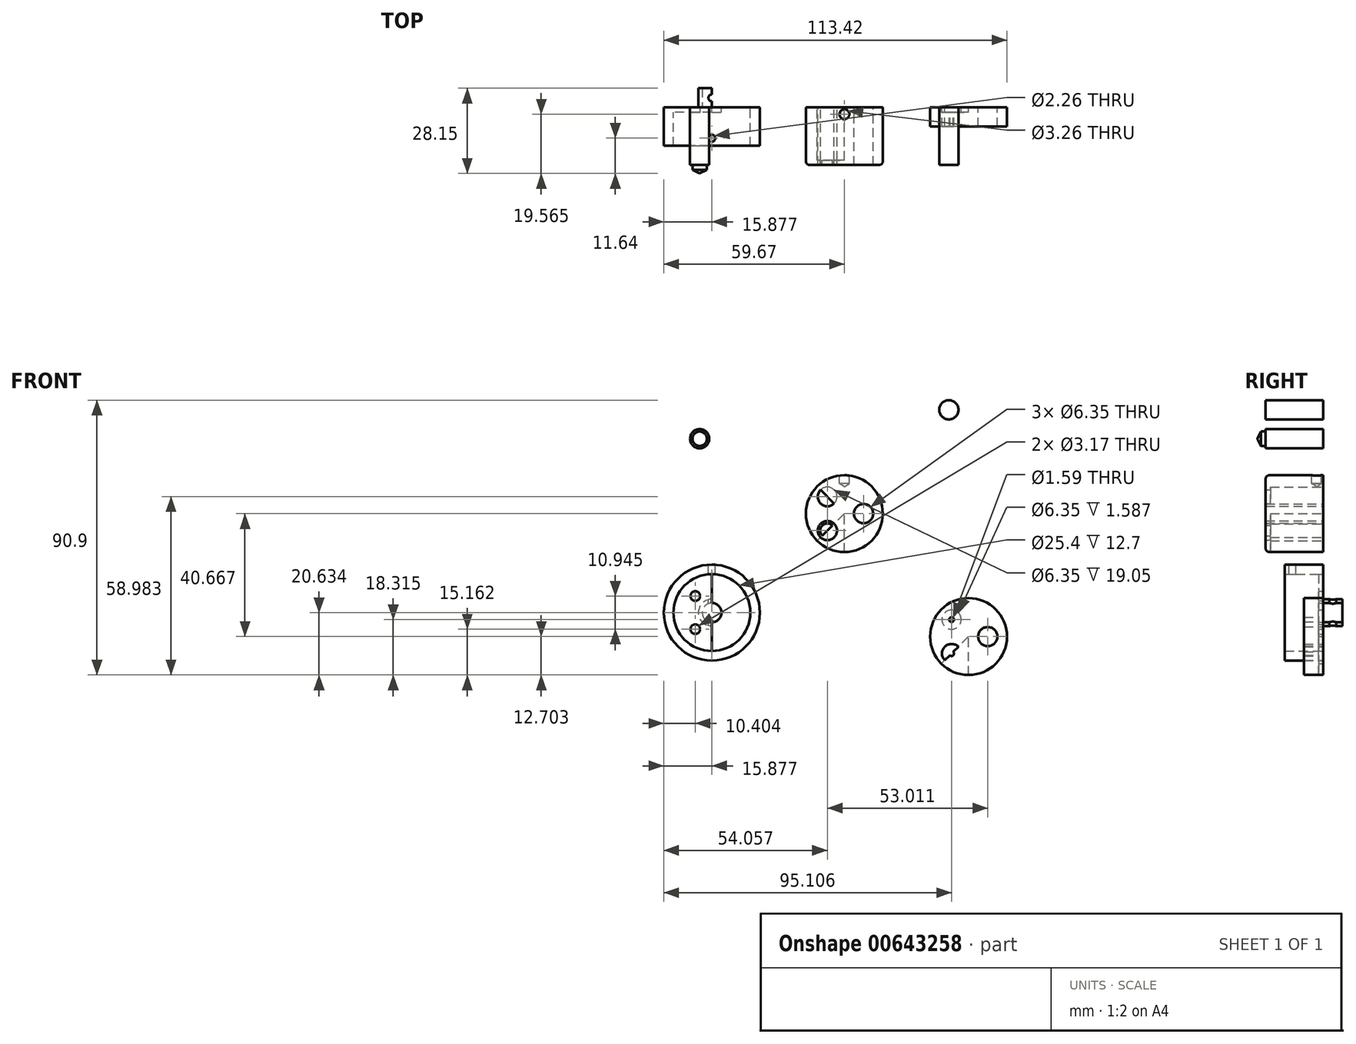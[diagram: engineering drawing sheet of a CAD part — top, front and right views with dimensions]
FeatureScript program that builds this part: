
annotation { "Feature Type Name" : "Feature", "Feature Type Description" : "" }
export const myFeature = defineFeature(function(context is Context, id is Id, definition is map)
    precondition{}
    {
        {
            var Q0;
            Q0=qCreatedBy(makeId("Front.planeOp"),FACE);
            var sketch = newSketch(context, id + "F0", { "sketchPlane" : qUnion([Q0])});
            skCircle(sketch, "E0", {"center": v(0, 0) * mm, "radius": 12.7 * mm});
            skLineSegment(sketch, "E1", {"start": v(0, 0) * mm, "end": v(12.7, 0) * mm});
            skLineSegment(sketch, "E2", {"start": v(12.7, 0) * mm, "end": v(0, 0) * mm});
            skLineSegment(sketch, "E3", {"start": v(0, 12.7) * mm, "end": v(0, 0) * mm});
            skLineSegment(sketch, "E4", {"start": v(0, -12.7) * mm, "end": v(0, 0) * mm});
            skLineSegment(sketch, "E5", {"start": v(-12.7, 0) * mm, "end": v(0, 0) * mm});
            skLineSegment(sketch, "E6", {"start": v(0, 12.7) * mm, "end": v(-12.7, 0) * mm});
            skLineSegment(sketch, "E7", {"start": v(-12.7, 0) * mm, "end": v(0, -12.7) * mm});
            skLineSegment(sketch, "E8", {"start": v(0, 0) * mm, "end": v(-8.98, -8.98) * mm});
            skLineSegment(sketch, "E9", {"start": v(-8.98, -8.98) * mm, "end": v(-8.98, 8.98) * mm});
            skLineSegment(sketch, "E10", {"start": v(-8.98, 8.98) * mm, "end": v(0, 0) * mm});
            skCircle(sketch, "E11", {"center": v(6.35, 0) * mm, "radius": 3.18 * mm});
            skCircle(sketch, "E12", {"center": v(6.35, 0) * mm, "radius": 2.38 * mm});
            skCircle(sketch, "E13", {"center": v(-5.61, 5.61) * mm, "radius": 3.18 * mm});
            skCircle(sketch, "E14", {"center": v(-5.61, -5.61) * mm, "radius": 3.18 * mm});
            skCircle(sketch, "E15", {"center": v(-5.61, 5.61) * mm, "radius": 2.38 * mm});
            skCircle(sketch, "E16", {"center": v(-5.61, -5.61) * mm, "radius": 2.38 * mm});
            skSolve(sketch);
        }
        {
            var Q0;
            {var subQ0=sQuery(id+"F0.wireOp",EDGE,"E4");Q0=makeQuery(id+"F0.imprint","IMPRINT",FACE,{"disambiguationData":[TD([[makeQuery(id+"F0.imprint","IMPRINT",EDGE,{"derivedFrom":subQ0}),-1.0]])]});}
            var Q1;
            {var subQ0=sQuery(id+"F0.wireOp",EDGE,"E3");Q1=makeQuery(id+"F0.imprint","IMPRINT",FACE,{"disambiguationData":[TD([[makeQuery(id+"F0.imprint","IMPRINT",EDGE,{"derivedFrom":subQ0}),1.0]])]});}
            var Q2;
            {var subQ0=sQuery(id+"F0.wireOp",EDGE,"E12");var subQ1=sQuery(id+"F0.wireOp",EDGE,"E2");var subQ2=makeQuery(id+"F0.imprint","INTERSECT",VERTEX,{"disambiguationData":[OD(0.0)],"derivedFrom":[subQ1,subQ0]});Q2=makeQuery(id+"F0.imprint","IMPRINT",FACE,{"disambiguationData":[TD([[makeQuery(id+"F0.imprint","IMPRINT",EDGE,{"disambiguationData":[TD([[subQ2,-1.0]])],"derivedFrom":subQ1}),1.0]])]});}
            var Q3;
            {var subQ0=sQuery(id+"F0.wireOp",EDGE,"E12");var subQ1=sQuery(id+"F0.wireOp",EDGE,"E2");var subQ2=makeQuery(id+"F0.imprint","INTERSECT",VERTEX,{"disambiguationData":[OD(0.0)],"derivedFrom":[subQ1,subQ0]});Q3=makeQuery(id+"F0.imprint","IMPRINT",FACE,{"disambiguationData":[TD([[makeQuery(id+"F0.imprint","IMPRINT",EDGE,{"disambiguationData":[TD([[subQ2,-1.0]])],"derivedFrom":subQ1}),-1.0]])]});}
            var Q4;
            {var subQ0=sQuery(id+"F0.wireOp",EDGE,"E11");var subQ1=sQuery(id+"F0.wireOp",EDGE,"E2");var subQ2=makeQuery(id+"F0.imprint","INTERSECT",VERTEX,{"disambiguationData":[OD(0.0)],"derivedFrom":[subQ1,subQ0]});Q4=makeQuery(id+"F0.imprint","IMPRINT",FACE,{"disambiguationData":[TD([[makeQuery(id+"F0.imprint","IMPRINT",EDGE,{"disambiguationData":[TD([[subQ2,-1.0]])],"derivedFrom":subQ1}),1.0]])]});}
            var Q5;
            {var subQ0=sQuery(id+"F0.wireOp",EDGE,"E11");var subQ1=sQuery(id+"F0.wireOp",EDGE,"E2");var subQ2=makeQuery(id+"F0.imprint","INTERSECT",VERTEX,{"disambiguationData":[OD(0.0)],"derivedFrom":[subQ1,subQ0]});Q5=makeQuery(id+"F0.imprint","IMPRINT",FACE,{"disambiguationData":[TD([[makeQuery(id+"F0.imprint","IMPRINT",EDGE,{"disambiguationData":[TD([[subQ2,-1.0]])],"derivedFrom":subQ1}),-1.0]])]});}
            var Q6;
            {var subQ0=sQuery(id+"F0.wireOp",EDGE,"E3");Q6=makeQuery(id+"F0.imprint","IMPRINT",FACE,{"disambiguationData":[TD([[makeQuery(id+"F0.imprint","IMPRINT",EDGE,{"derivedFrom":subQ0}),-1.0]])]});}
            var Q7;
            {var subQ0=sQuery(id+"F0.wireOp",EDGE,"E4");Q7=makeQuery(id+"F0.imprint","IMPRINT",FACE,{"disambiguationData":[TD([[makeQuery(id+"F0.imprint","IMPRINT",EDGE,{"derivedFrom":subQ0}),1.0]])]});}
            var Q8;
            {var subQ0=sQuery(id+"F0.wireOp",EDGE,"E7");var subQ5=sQuery(id+"F0.wireOp",EDGE,"E14");var subQ7=makeQuery(id+"F0.imprint","INTERSECT",VERTEX,{"disambiguationData":[OD(1.0)],"derivedFrom":[subQ0,subQ5]});Q8=makeQuery(id+"F0.imprint","IMPRINT",FACE,{"disambiguationData":[TD([[makeQuery(id+"F0.imprint","IMPRINT",EDGE,{"disambiguationData":[TD([[subQ7,1.0]])],"derivedFrom":subQ5}),-1.0]])]});}
            var Q9;
            {var subQ0=sQuery(id+"F0.wireOp",EDGE,"E8");var subQ1=sQuery(id+"F0.wireOp",EDGE,"E7");var subQ2=makeQuery(id+"F0.imprint","INTERSECT",VERTEX,{"derivedFrom":[subQ1,subQ0]});Q9=makeQuery(id+"F0.imprint","IMPRINT",FACE,{"disambiguationData":[TD([[makeQuery(id+"F0.imprint","IMPRINT",EDGE,{"disambiguationData":[TD([[subQ2,-1.0]])],"derivedFrom":subQ1}),1.0]])]});}
            var Q10;
            {var subQ0=sQuery(id+"F0.wireOp",EDGE,"E16");var subQ1=sQuery(id+"F0.wireOp",EDGE,"E7");var subQ2=makeQuery(id+"F0.imprint","INTERSECT",VERTEX,{"disambiguationData":[OD(0.0)],"derivedFrom":[subQ1,subQ0]});Q10=makeQuery(id+"F0.imprint","IMPRINT",FACE,{"disambiguationData":[TD([[makeQuery(id+"F0.imprint","IMPRINT",EDGE,{"disambiguationData":[TD([[subQ2,-1.0]])],"derivedFrom":subQ1}),1.0]])]});}
            var Q11;
            {var subQ0=sQuery(id+"F0.wireOp",EDGE,"E8");var subQ1=sQuery(id+"F0.wireOp",EDGE,"E7");var subQ2=makeQuery(id+"F0.imprint","INTERSECT",VERTEX,{"derivedFrom":[subQ1,subQ0]});Q11=makeQuery(id+"F0.imprint","IMPRINT",FACE,{"disambiguationData":[TD([[makeQuery(id+"F0.imprint","IMPRINT",EDGE,{"disambiguationData":[TD([[subQ2,-1.0]])],"derivedFrom":subQ1}),-1.0]])]});}
            var Q12;
            {var subQ0=sQuery(id+"F0.wireOp",EDGE,"E16");var subQ1=sQuery(id+"F0.wireOp",EDGE,"E7");var subQ2=makeQuery(id+"F0.imprint","INTERSECT",VERTEX,{"disambiguationData":[OD(0.0)],"derivedFrom":[subQ1,subQ0]});Q12=makeQuery(id+"F0.imprint","IMPRINT",FACE,{"disambiguationData":[TD([[makeQuery(id+"F0.imprint","IMPRINT",EDGE,{"disambiguationData":[TD([[subQ2,-1.0]])],"derivedFrom":subQ1}),-1.0]])]});}
            var Q13;
            {var subQ0=sQuery(id+"F0.wireOp",EDGE,"E9");var subQ3=sQuery(id+"F0.wireOp",EDGE,"E7");var subQ4=makeQuery(id+"F0.imprint","INTERSECT",VERTEX,{"derivedFrom":[subQ3,subQ0]});Q13=makeQuery(id+"F0.imprint","IMPRINT",FACE,{"disambiguationData":[TD([[makeQuery(id+"F0.imprint","IMPRINT",EDGE,{"disambiguationData":[TD([[subQ4,-1.0]])],"derivedFrom":subQ3}),1.0]])]});}
            var Q14;
            {var subQ3=sQuery(id+"F0.wireOp",EDGE,"E6");var subQ5=sQuery(id+"F0.wireOp",EDGE,"E13");var subQ6=makeQuery(id+"F0.imprint","INTERSECT",VERTEX,{"disambiguationData":[OD(1.0)],"derivedFrom":[subQ3,subQ5]});Q14=makeQuery(id+"F0.imprint","IMPRINT",FACE,{"disambiguationData":[TD([[makeQuery(id+"F0.imprint","IMPRINT",EDGE,{"disambiguationData":[TD([[subQ6,-1.0]])],"derivedFrom":subQ3}),1.0]])]});}
            var Q15;
            {var subQ0=sQuery(id+"F0.wireOp",EDGE,"E10");var subQ1=sQuery(id+"F0.wireOp",EDGE,"E6");var subQ2=makeQuery(id+"F0.imprint","INTERSECT",VERTEX,{"derivedFrom":[subQ1,subQ0]});Q15=makeQuery(id+"F0.imprint","IMPRINT",FACE,{"disambiguationData":[TD([[makeQuery(id+"F0.imprint","IMPRINT",EDGE,{"disambiguationData":[TD([[subQ2,-1.0]])],"derivedFrom":subQ1}),1.0]])]});}
            var Q16;
            {var subQ0=sQuery(id+"F0.wireOp",EDGE,"E15");var subQ1=sQuery(id+"F0.wireOp",EDGE,"E6");var subQ2=makeQuery(id+"F0.imprint","INTERSECT",VERTEX,{"disambiguationData":[OD(0.0)],"derivedFrom":[subQ1,subQ0]});Q16=makeQuery(id+"F0.imprint","IMPRINT",FACE,{"disambiguationData":[TD([[makeQuery(id+"F0.imprint","IMPRINT",EDGE,{"disambiguationData":[TD([[subQ2,-1.0]])],"derivedFrom":subQ1}),1.0]])]});}
            var Q17;
            {var subQ0=sQuery(id+"F0.wireOp",EDGE,"E15");var subQ1=sQuery(id+"F0.wireOp",EDGE,"E6");var subQ2=makeQuery(id+"F0.imprint","INTERSECT",VERTEX,{"disambiguationData":[OD(0.0)],"derivedFrom":[subQ1,subQ0]});Q17=makeQuery(id+"F0.imprint","IMPRINT",FACE,{"disambiguationData":[TD([[makeQuery(id+"F0.imprint","IMPRINT",EDGE,{"disambiguationData":[TD([[subQ2,-1.0]])],"derivedFrom":subQ1}),-1.0]])]});}
            var Q18;
            {var subQ0=sQuery(id+"F0.wireOp",EDGE,"E10");var subQ1=sQuery(id+"F0.wireOp",EDGE,"E6");var subQ2=makeQuery(id+"F0.imprint","INTERSECT",VERTEX,{"derivedFrom":[subQ1,subQ0]});Q18=makeQuery(id+"F0.imprint","IMPRINT",FACE,{"disambiguationData":[TD([[makeQuery(id+"F0.imprint","IMPRINT",EDGE,{"disambiguationData":[TD([[subQ2,-1.0]])],"derivedFrom":subQ1}),-1.0]])]});}
            var Q19;
            {var subQ0=sQuery(id+"F0.wireOp",EDGE,"E13");var subQ1=sQuery(id+"F0.wireOp",EDGE,"E6");var subQ2=makeQuery(id+"F0.imprint","INTERSECT",VERTEX,{"disambiguationData":[OD(0.0)],"derivedFrom":[subQ1,subQ0]});Q19=makeQuery(id+"F0.imprint","IMPRINT",FACE,{"disambiguationData":[TD([[makeQuery(id+"F0.imprint","IMPRINT",EDGE,{"disambiguationData":[TD([[subQ2,-1.0]])],"derivedFrom":subQ1}),-1.0]])]});}
            var Q20;
            {var subQ0=sQuery(id+"F0.wireOp",EDGE,"E13");var subQ1=sQuery(id+"F0.wireOp",EDGE,"E6");var subQ2=makeQuery(id+"F0.imprint","INTERSECT",VERTEX,{"disambiguationData":[OD(0.0)],"derivedFrom":[subQ1,subQ0]});Q20=makeQuery(id+"F0.imprint","IMPRINT",FACE,{"disambiguationData":[TD([[makeQuery(id+"F0.imprint","IMPRINT",EDGE,{"disambiguationData":[TD([[subQ2,-1.0]])],"derivedFrom":subQ1}),1.0]])]});}
            var Q21;
            {var subQ0=sQuery(id+"F0.wireOp",EDGE,"E15");var subQ1=sQuery(id+"F0.wireOp",EDGE,"E6");var subQ2=makeQuery(id+"F0.imprint","INTERSECT",VERTEX,{"disambiguationData":[OD(1.0)],"derivedFrom":[subQ1,subQ0]});Q21=makeQuery(id+"F0.imprint","IMPRINT",FACE,{"disambiguationData":[TD([[makeQuery(id+"F0.imprint","IMPRINT",EDGE,{"disambiguationData":[TD([[subQ2,-1.0]])],"derivedFrom":subQ1}),1.0]])]});}
            var Q22;
            {var subQ0=sQuery(id+"F0.wireOp",EDGE,"E15");var subQ1=sQuery(id+"F0.wireOp",EDGE,"E6");var subQ2=makeQuery(id+"F0.imprint","INTERSECT",VERTEX,{"disambiguationData":[OD(1.0)],"derivedFrom":[subQ1,subQ0]});Q22=makeQuery(id+"F0.imprint","IMPRINT",FACE,{"disambiguationData":[TD([[makeQuery(id+"F0.imprint","IMPRINT",EDGE,{"disambiguationData":[TD([[subQ2,-1.0]])],"derivedFrom":subQ1}),-1.0]])]});}
            var Q23;
            {var subQ0=sQuery(id+"F0.wireOp",EDGE,"E13");var subQ1=sQuery(id+"F0.wireOp",EDGE,"E6");var subQ2=makeQuery(id+"F0.imprint","INTERSECT",VERTEX,{"disambiguationData":[OD(1.0)],"derivedFrom":[subQ1,subQ0]});Q23=makeQuery(id+"F0.imprint","IMPRINT",FACE,{"disambiguationData":[TD([[makeQuery(id+"F0.imprint","IMPRINT",EDGE,{"disambiguationData":[TD([[subQ2,-1.0]])],"derivedFrom":subQ1}),-1.0]])]});}
            var Q24;
            {var subQ0=sQuery(id+"F0.wireOp",EDGE,"E6");var subQ5=sQuery(id+"F0.wireOp",EDGE,"E13");var subQ6=makeQuery(id+"F0.imprint","INTERSECT",VERTEX,{"disambiguationData":[OD(0.0)],"derivedFrom":[subQ0,subQ5]});Q24=makeQuery(id+"F0.imprint","IMPRINT",FACE,{"disambiguationData":[TD([[makeQuery(id+"F0.imprint","IMPRINT",EDGE,{"disambiguationData":[TD([[subQ6,-1.0]])],"derivedFrom":subQ5}),-1.0]])]});}
            var Q25;
            {var subQ0=sQuery(id+"F0.wireOp",EDGE,"E6");var subQ3=sQuery(id+"F0.wireOp",EDGE,"E9");var subQ5=makeQuery(id+"F0.imprint","INTERSECT",VERTEX,{"derivedFrom":[subQ0,subQ3]});Q25=makeQuery(id+"F0.imprint","IMPRINT",FACE,{"disambiguationData":[TD([[makeQuery(id+"F0.imprint","IMPRINT",EDGE,{"disambiguationData":[TD([[subQ5,-1.0]])],"derivedFrom":subQ3}),1.0]])]});}
            var Q26;
            {var subQ1=sQuery(id+"F0.wireOp",EDGE,"E5");var subQ3=sQuery(id+"F0.wireOp",EDGE,"E9");var subQ4=makeQuery(id+"F0.imprint","INTERSECT",VERTEX,{"derivedFrom":[subQ1,subQ3]});Q26=makeQuery(id+"F0.imprint","IMPRINT",FACE,{"disambiguationData":[TD([[makeQuery(id+"F0.imprint","IMPRINT",EDGE,{"disambiguationData":[TD([[subQ4,-1.0]])],"derivedFrom":subQ3}),1.0]])]});}
            var Q27;
            {var subQ1=sQuery(id+"F0.wireOp",EDGE,"E5");var subQ3=sQuery(id+"F0.wireOp",EDGE,"E9");var subQ4=makeQuery(id+"F0.imprint","INTERSECT",VERTEX,{"derivedFrom":[subQ1,subQ3]});Q27=makeQuery(id+"F0.imprint","IMPRINT",FACE,{"disambiguationData":[TD([[makeQuery(id+"F0.imprint","IMPRINT",EDGE,{"disambiguationData":[TD([[subQ4,1.0]])],"derivedFrom":subQ3}),1.0]])]});}
            var Q28;
            {var subQ0=sQuery(id+"F0.wireOp",EDGE,"E7");var subQ3=sQuery(id+"F0.wireOp",EDGE,"E9");var subQ5=makeQuery(id+"F0.imprint","INTERSECT",VERTEX,{"derivedFrom":[subQ0,subQ3]});Q28=makeQuery(id+"F0.imprint","IMPRINT",FACE,{"disambiguationData":[TD([[makeQuery(id+"F0.imprint","IMPRINT",EDGE,{"disambiguationData":[TD([[subQ5,1.0]])],"derivedFrom":subQ3}),1.0]])]});}
            var Q29;
            {var subQ0=sQuery(id+"F0.wireOp",EDGE,"E9");var subQ1=sQuery(id+"F0.wireOp",EDGE,"E7");var subQ2=makeQuery(id+"F0.imprint","INTERSECT",VERTEX,{"derivedFrom":[subQ1,subQ0]});Q29=makeQuery(id+"F0.imprint","IMPRINT",FACE,{"disambiguationData":[TD([[makeQuery(id+"F0.imprint","IMPRINT",EDGE,{"disambiguationData":[TD([[subQ2,-1.0]])],"derivedFrom":subQ1}),-1.0]])]});}
            var Q30;
            {var subQ0=sQuery(id+"F0.wireOp",EDGE,"E14");var subQ1=sQuery(id+"F0.wireOp",EDGE,"E7");var subQ2=makeQuery(id+"F0.imprint","INTERSECT",VERTEX,{"disambiguationData":[OD(0.0)],"derivedFrom":[subQ1,subQ0]});Q30=makeQuery(id+"F0.imprint","IMPRINT",FACE,{"disambiguationData":[TD([[makeQuery(id+"F0.imprint","IMPRINT",EDGE,{"disambiguationData":[TD([[subQ2,-1.0]])],"derivedFrom":subQ1}),1.0]])]});}
            var Q31;
            {var subQ0=sQuery(id+"F0.wireOp",EDGE,"E14");var subQ1=sQuery(id+"F0.wireOp",EDGE,"E7");var subQ2=makeQuery(id+"F0.imprint","INTERSECT",VERTEX,{"disambiguationData":[OD(0.0)],"derivedFrom":[subQ1,subQ0]});Q31=makeQuery(id+"F0.imprint","IMPRINT",FACE,{"disambiguationData":[TD([[makeQuery(id+"F0.imprint","IMPRINT",EDGE,{"disambiguationData":[TD([[subQ2,-1.0]])],"derivedFrom":subQ1}),-1.0]])]});}
            var Q32;
            {var subQ0=sQuery(id+"F0.wireOp",EDGE,"E16");var subQ1=sQuery(id+"F0.wireOp",EDGE,"E7");var subQ2=makeQuery(id+"F0.imprint","INTERSECT",VERTEX,{"disambiguationData":[OD(1.0)],"derivedFrom":[subQ1,subQ0]});Q32=makeQuery(id+"F0.imprint","IMPRINT",FACE,{"disambiguationData":[TD([[makeQuery(id+"F0.imprint","IMPRINT",EDGE,{"disambiguationData":[TD([[subQ2,-1.0]])],"derivedFrom":subQ1}),1.0]])]});}
            var Q33;
            {var subQ0=sQuery(id+"F0.wireOp",EDGE,"E16");var subQ1=sQuery(id+"F0.wireOp",EDGE,"E7");var subQ2=makeQuery(id+"F0.imprint","INTERSECT",VERTEX,{"disambiguationData":[OD(1.0)],"derivedFrom":[subQ1,subQ0]});Q33=makeQuery(id+"F0.imprint","IMPRINT",FACE,{"disambiguationData":[TD([[makeQuery(id+"F0.imprint","IMPRINT",EDGE,{"disambiguationData":[TD([[subQ2,-1.0]])],"derivedFrom":subQ1}),-1.0]])]});}
            extrude(context, id + "F1", {"entities" : qUnion([Q0, Q1, Q2, Q3, Q4, Q5, Q6, Q7, Q8, Q9, Q10, Q11, Q12, Q13, Q14, Q15, Q16, Q17, Q18, Q19, Q20, Q21, Q22, Q23, Q24, Q25, Q26, Q27, Q28, Q29, Q30, Q31, Q32, Q33]), "depth" : 19.05 * mm, "offsetDistance" : 25.4 * mm});
        }
        {
            var Q0;
            {var subQ0=sQuery(id+"F0.wireOp",EDGE,"E12");var subQ1=sQuery(id+"F0.wireOp",EDGE,"E2");var subQ2=makeQuery(id+"F0.imprint","INTERSECT",VERTEX,{"disambiguationData":[OD(0.0)],"derivedFrom":[subQ1,subQ0]});Q0=makeQuery(id+"F0.imprint","IMPRINT",FACE,{"disambiguationData":[TD([[makeQuery(id+"F0.imprint","IMPRINT",EDGE,{"disambiguationData":[TD([[subQ2,-1.0]])],"derivedFrom":subQ1}),-1.0]])]});}
            var Q1;
            {var subQ0=sQuery(id+"F0.wireOp",EDGE,"E12");var subQ1=sQuery(id+"F0.wireOp",EDGE,"E2");var subQ2=makeQuery(id+"F0.imprint","INTERSECT",VERTEX,{"disambiguationData":[OD(0.0)],"derivedFrom":[subQ1,subQ0]});Q1=makeQuery(id+"F0.imprint","IMPRINT",FACE,{"disambiguationData":[TD([[makeQuery(id+"F0.imprint","IMPRINT",EDGE,{"disambiguationData":[TD([[subQ2,-1.0]])],"derivedFrom":subQ1}),1.0]])]});}
            var Q2;
            {var subQ0=sQuery(id+"F0.wireOp",EDGE,"E15");var subQ1=sQuery(id+"F0.wireOp",EDGE,"E6");var subQ2=makeQuery(id+"F0.imprint","INTERSECT",VERTEX,{"disambiguationData":[OD(0.0)],"derivedFrom":[subQ1,subQ0]});Q2=makeQuery(id+"F0.imprint","IMPRINT",FACE,{"disambiguationData":[TD([[makeQuery(id+"F0.imprint","IMPRINT",EDGE,{"disambiguationData":[TD([[subQ2,-1.0]])],"derivedFrom":subQ1}),1.0]])]});}
            var Q3;
            {var subQ0=sQuery(id+"F0.wireOp",EDGE,"E10");var subQ1=sQuery(id+"F0.wireOp",EDGE,"E6");var subQ2=makeQuery(id+"F0.imprint","INTERSECT",VERTEX,{"derivedFrom":[subQ1,subQ0]});Q3=makeQuery(id+"F0.imprint","IMPRINT",FACE,{"disambiguationData":[TD([[makeQuery(id+"F0.imprint","IMPRINT",EDGE,{"disambiguationData":[TD([[subQ2,-1.0]])],"derivedFrom":subQ1}),1.0]])]});}
            var Q4;
            {var subQ0=sQuery(id+"F0.wireOp",EDGE,"E10");var subQ1=sQuery(id+"F0.wireOp",EDGE,"E6");var subQ2=makeQuery(id+"F0.imprint","INTERSECT",VERTEX,{"derivedFrom":[subQ1,subQ0]});Q4=makeQuery(id+"F0.imprint","IMPRINT",FACE,{"disambiguationData":[TD([[makeQuery(id+"F0.imprint","IMPRINT",EDGE,{"disambiguationData":[TD([[subQ2,-1.0]])],"derivedFrom":subQ1}),-1.0]])]});}
            var Q5;
            {var subQ0=sQuery(id+"F0.wireOp",EDGE,"E15");var subQ1=sQuery(id+"F0.wireOp",EDGE,"E6");var subQ2=makeQuery(id+"F0.imprint","INTERSECT",VERTEX,{"disambiguationData":[OD(0.0)],"derivedFrom":[subQ1,subQ0]});Q5=makeQuery(id+"F0.imprint","IMPRINT",FACE,{"disambiguationData":[TD([[makeQuery(id+"F0.imprint","IMPRINT",EDGE,{"disambiguationData":[TD([[subQ2,-1.0]])],"derivedFrom":subQ1}),-1.0]])]});}
            var Q6;
            {var subQ0=sQuery(id+"F0.wireOp",EDGE,"E16");var subQ1=sQuery(id+"F0.wireOp",EDGE,"E7");var subQ2=makeQuery(id+"F0.imprint","INTERSECT",VERTEX,{"disambiguationData":[OD(0.0)],"derivedFrom":[subQ1,subQ0]});Q6=makeQuery(id+"F0.imprint","IMPRINT",FACE,{"disambiguationData":[TD([[makeQuery(id+"F0.imprint","IMPRINT",EDGE,{"disambiguationData":[TD([[subQ2,-1.0]])],"derivedFrom":subQ1}),1.0]])]});}
            var Q7;
            {var subQ0=sQuery(id+"F0.wireOp",EDGE,"E8");var subQ1=sQuery(id+"F0.wireOp",EDGE,"E7");var subQ2=makeQuery(id+"F0.imprint","INTERSECT",VERTEX,{"derivedFrom":[subQ1,subQ0]});Q7=makeQuery(id+"F0.imprint","IMPRINT",FACE,{"disambiguationData":[TD([[makeQuery(id+"F0.imprint","IMPRINT",EDGE,{"disambiguationData":[TD([[subQ2,-1.0]])],"derivedFrom":subQ1}),1.0]])]});}
            var Q8;
            {var subQ0=sQuery(id+"F0.wireOp",EDGE,"E8");var subQ1=sQuery(id+"F0.wireOp",EDGE,"E7");var subQ2=makeQuery(id+"F0.imprint","INTERSECT",VERTEX,{"derivedFrom":[subQ1,subQ0]});Q8=makeQuery(id+"F0.imprint","IMPRINT",FACE,{"disambiguationData":[TD([[makeQuery(id+"F0.imprint","IMPRINT",EDGE,{"disambiguationData":[TD([[subQ2,-1.0]])],"derivedFrom":subQ1}),-1.0]])]});}
            var Q9;
            {var subQ0=sQuery(id+"F0.wireOp",EDGE,"E16");var subQ1=sQuery(id+"F0.wireOp",EDGE,"E7");var subQ2=makeQuery(id+"F0.imprint","INTERSECT",VERTEX,{"disambiguationData":[OD(0.0)],"derivedFrom":[subQ1,subQ0]});Q9=makeQuery(id+"F0.imprint","IMPRINT",FACE,{"disambiguationData":[TD([[makeQuery(id+"F0.imprint","IMPRINT",EDGE,{"disambiguationData":[TD([[subQ2,-1.0]])],"derivedFrom":subQ1}),-1.0]])]});}
            extrude(context, id + "F2", {"entities" : qUnion([Q0, Q1, Q2, Q3, Q4, Q5, Q6, Q7, Q8, Q9]), "operationType" : NewBodyOperationType.REMOVE, "endBound" : BoundingType.UP_TO_NEXT, "depth" : 25.4 * mm, "offsetDistance" : 25.4 * mm});
        }
        {
            var Q0;
            {var subQ0=sQuery(id+"F0.wireOp",EDGE,"E13");var subQ1=sQuery(id+"F0.wireOp",EDGE,"E6");var subQ2=makeQuery(id+"F0.imprint","INTERSECT",VERTEX,{"disambiguationData":[OD(0.0)],"derivedFrom":[subQ1,subQ0]});Q0=makeQuery(id+"F0.imprint","IMPRINT",FACE,{"disambiguationData":[TD([[makeQuery(id+"F0.imprint","IMPRINT",EDGE,{"disambiguationData":[TD([[subQ2,-1.0]])],"derivedFrom":subQ1}),-1.0]])]});}
            var Q1;
            {var subQ0=sQuery(id+"F0.wireOp",EDGE,"E15");var subQ1=sQuery(id+"F0.wireOp",EDGE,"E6");var subQ2=makeQuery(id+"F0.imprint","INTERSECT",VERTEX,{"disambiguationData":[OD(1.0)],"derivedFrom":[subQ1,subQ0]});Q1=makeQuery(id+"F0.imprint","IMPRINT",FACE,{"disambiguationData":[TD([[makeQuery(id+"F0.imprint","IMPRINT",EDGE,{"disambiguationData":[TD([[subQ2,-1.0]])],"derivedFrom":subQ1}),-1.0]])]});}
            var Q2;
            {var subQ0=sQuery(id+"F0.wireOp",EDGE,"E15");var subQ1=sQuery(id+"F0.wireOp",EDGE,"E6");var subQ2=makeQuery(id+"F0.imprint","INTERSECT",VERTEX,{"disambiguationData":[OD(1.0)],"derivedFrom":[subQ1,subQ0]});Q2=makeQuery(id+"F0.imprint","IMPRINT",FACE,{"disambiguationData":[TD([[makeQuery(id+"F0.imprint","IMPRINT",EDGE,{"disambiguationData":[TD([[subQ2,-1.0]])],"derivedFrom":subQ1}),1.0]])]});}
            var Q3;
            {var subQ0=sQuery(id+"F0.wireOp",EDGE,"E13");var subQ1=sQuery(id+"F0.wireOp",EDGE,"E6");var subQ2=makeQuery(id+"F0.imprint","INTERSECT",VERTEX,{"disambiguationData":[OD(0.0)],"derivedFrom":[subQ1,subQ0]});Q3=makeQuery(id+"F0.imprint","IMPRINT",FACE,{"disambiguationData":[TD([[makeQuery(id+"F0.imprint","IMPRINT",EDGE,{"disambiguationData":[TD([[subQ2,-1.0]])],"derivedFrom":subQ1}),1.0]])]});}
            var Q4;
            {var subQ0=sQuery(id+"F0.wireOp",EDGE,"E14");var subQ1=sQuery(id+"F0.wireOp",EDGE,"E7");var subQ2=makeQuery(id+"F0.imprint","INTERSECT",VERTEX,{"disambiguationData":[OD(0.0)],"derivedFrom":[subQ1,subQ0]});Q4=makeQuery(id+"F0.imprint","IMPRINT",FACE,{"disambiguationData":[TD([[makeQuery(id+"F0.imprint","IMPRINT",EDGE,{"disambiguationData":[TD([[subQ2,-1.0]])],"derivedFrom":subQ1}),1.0]])]});}
            var Q5;
            {var subQ0=sQuery(id+"F0.wireOp",EDGE,"E14");var subQ1=sQuery(id+"F0.wireOp",EDGE,"E7");var subQ2=makeQuery(id+"F0.imprint","INTERSECT",VERTEX,{"disambiguationData":[OD(0.0)],"derivedFrom":[subQ1,subQ0]});Q5=makeQuery(id+"F0.imprint","IMPRINT",FACE,{"disambiguationData":[TD([[makeQuery(id+"F0.imprint","IMPRINT",EDGE,{"disambiguationData":[TD([[subQ2,-1.0]])],"derivedFrom":subQ1}),-1.0]])]});}
            var Q6;
            {var subQ0=sQuery(id+"F0.wireOp",EDGE,"E16");var subQ1=sQuery(id+"F0.wireOp",EDGE,"E7");var subQ2=makeQuery(id+"F0.imprint","INTERSECT",VERTEX,{"disambiguationData":[OD(1.0)],"derivedFrom":[subQ1,subQ0]});Q6=makeQuery(id+"F0.imprint","IMPRINT",FACE,{"disambiguationData":[TD([[makeQuery(id+"F0.imprint","IMPRINT",EDGE,{"disambiguationData":[TD([[subQ2,-1.0]])],"derivedFrom":subQ1}),-1.0]])]});}
            var Q7;
            {var subQ0=sQuery(id+"F0.wireOp",EDGE,"E16");var subQ1=sQuery(id+"F0.wireOp",EDGE,"E7");var subQ2=makeQuery(id+"F0.imprint","INTERSECT",VERTEX,{"disambiguationData":[OD(1.0)],"derivedFrom":[subQ1,subQ0]});Q7=makeQuery(id+"F0.imprint","IMPRINT",FACE,{"disambiguationData":[TD([[makeQuery(id+"F0.imprint","IMPRINT",EDGE,{"disambiguationData":[TD([[subQ2,-1.0]])],"derivedFrom":subQ1}),1.0]])]});}
            var Q8;
            {var subQ0=sQuery(id+"F0.wireOp",EDGE,"E11");var subQ1=sQuery(id+"F0.wireOp",EDGE,"E2");var subQ2=makeQuery(id+"F0.imprint","INTERSECT",VERTEX,{"disambiguationData":[OD(0.0)],"derivedFrom":[subQ1,subQ0]});Q8=makeQuery(id+"F0.imprint","IMPRINT",FACE,{"disambiguationData":[TD([[makeQuery(id+"F0.imprint","IMPRINT",EDGE,{"disambiguationData":[TD([[subQ2,-1.0]])],"derivedFrom":subQ1}),1.0]])]});}
            var Q9;
            {var subQ0=sQuery(id+"F0.wireOp",EDGE,"E11");var subQ1=sQuery(id+"F0.wireOp",EDGE,"E2");var subQ2=makeQuery(id+"F0.imprint","INTERSECT",VERTEX,{"disambiguationData":[OD(0.0)],"derivedFrom":[subQ1,subQ0]});Q9=makeQuery(id+"F0.imprint","IMPRINT",FACE,{"disambiguationData":[TD([[makeQuery(id+"F0.imprint","IMPRINT",EDGE,{"disambiguationData":[TD([[subQ2,-1.0]])],"derivedFrom":subQ1}),-1.0]])]});}
            extrude(context, id + "F3", {"entities" : qUnion([Q0, Q1, Q2, Q3, Q4, Q5, Q6, Q7, Q8, Q9]), "operationType" : NewBodyOperationType.REMOVE, "depth" : 17.46 * mm, "offsetDistance" : 25.4 * mm});
        }
        {
            var Q0;
            Q0=qCreatedBy(makeId("Front.planeOp"),FACE);
            var sketch = newSketch(context, id + "F4", { "sketchPlane" : qUnion([Q0])});
            skCircle(sketch, "E17", {"center": v(-47.82, 24.77) * mm, "radius": 3.18 * mm});
            skSolve(sketch);
        }
        {
            var Q0;
            Q0 = qSketchRegion(id + "F4", true);
            extrude(context, id + "F5", {"entities" : qUnion([Q0]), "depth" : 19.05 * mm, "offsetDistance" : 25.4 * mm});
        }
        {
            var Q0;
            Q0=makeQuery(id+"F5.opExtrude","CAP_FACE",FACE,{"disambiguationData":[OSD([sQuery(id+"F4.wireOp",EDGE,"E17")])],"isStart":false});
            var sketch = newSketch(context, id + "F6", { "sketchPlane" : qUnion([Q0])});
            skCircle(sketch, "E18", {"center": v(-47.82, 24.77) * mm, "radius": 2.38 * mm});
            skSolve(sketch);
        }
        {
            var Q0;
            Q0=makeQuery(id+"F6.imprint","IMPRINT",FACE,{"disambiguationData":[TD([[makeQuery(id+"F6.imprint","IMPRINT",EDGE,{"derivedFrom":sQuery(id+"F6.wireOp",EDGE,"E18")}),1.0]])]});
            extrude(context, id + "F7", {"entities" : qUnion([Q0]), "operationType" : NewBodyOperationType.ADD, "flatOperationType" : FlatOperationType.REMOVE, "depth" : 1.59 * mm, "offsetDistance" : 25.4 * mm, "domain" : OperationDomain.MODEL});
        }
        {
            var Q0;
            Q0=makeQuery(id+"F7.opExtrude","CAP_FACE",FACE,{"disambiguationData":[OSD([sQuery(id+"F6.wireOp",EDGE,"E18")])],"isStart":false});
            var sketch = newSketch(context, id + "F8", { "sketchPlane" : qUnion([Q0])});
            skCircle(sketch, "E19", {"center": v(-47.82, 24.77) * mm, "radius": 2.38 * mm});
            skSolve(sketch);
        }
        {
            var Q0;
            Q0 = qSketchRegion(id + "F8", true);
            extrude(context, id + "F9", {"entities" : qUnion([Q0]), "operationType" : NewBodyOperationType.ADD, "depth" : 1.59 * mm, "offsetDistance" : 25.4 * mm, "hasDraft" : true, "draftAngle" : 64 * degree, "draftPullDirection" : true});
        }
        {
            var Q0;
            Q0=qCreatedBy(makeId("Front.planeOp"),FACE);
            var sketch = newSketch(context, id + "F10", { "sketchPlane" : qUnion([Q0])});
            skCircle(sketch, "E20", {"center": v(34.53, 34.35) * mm, "radius": 3.18 * mm});
            skSolve(sketch);
        }
        {
            var Q0;
            Q0 = qSketchRegion(id + "F10", true);
            extrude(context, id + "F11", {"entities" : qUnion([Q0]), "depth" : 19.05 * mm, "offsetDistance" : 25.4 * mm});
        }
        {
            var Q0;
            Q0=qCreatedBy(makeId("Front.planeOp"),FACE);
            var sketch = newSketch(context, id + "F12", { "sketchPlane" : qUnion([Q0])});
            skCircle(sketch, "E21", {"center": v(41.05, -40.67) * mm, "radius": 12.7 * mm});
            skLineSegment(sketch, "E22", {"start": v(41.05, -40.67) * mm, "end": v(53.75, -40.67) * mm});
            skLineSegment(sketch, "E23", {"start": v(53.75, -40.67) * mm, "end": v(41.05, -40.67) * mm});
            skLineSegment(sketch, "E24", {"start": v(41.05, -27.97) * mm, "end": v(41.05, -40.67) * mm});
            skLineSegment(sketch, "E25", {"start": v(41.05, -53.37) * mm, "end": v(41.05, -40.67) * mm});
            skLineSegment(sketch, "E26", {"start": v(28.35, -40.67) * mm, "end": v(41.05, -40.67) * mm});
            skLineSegment(sketch, "E27", {"start": v(41.05, -27.97) * mm, "end": v(28.35, -40.67) * mm});
            skLineSegment(sketch, "E28", {"start": v(28.35, -40.67) * mm, "end": v(41.05, -53.37) * mm});
            skLineSegment(sketch, "E29", {"start": v(41.05, -40.67) * mm, "end": v(32.07, -49.65) * mm});
            skLineSegment(sketch, "E30", {"start": v(32.07, -49.65) * mm, "end": v(32.07, -31.69) * mm});
            skLineSegment(sketch, "E31", {"start": v(32.07, -31.69) * mm, "end": v(41.05, -40.67) * mm});
            skCircle(sketch, "E32", {"center": v(47.4, -40.67) * mm, "radius": 3.18 * mm});
            skCircle(sketch, "E33", {"center": v(47.4, -40.67) * mm, "radius": 0.8 * mm});
            skCircle(sketch, "E34", {"center": v(35.44, -35.05) * mm, "radius": 3.18 * mm});
            skCircle(sketch, "E35", {"center": v(35.44, -46.28) * mm, "radius": 3.18 * mm});
            skCircle(sketch, "E36", {"center": v(35.44, -35.05) * mm, "radius": 0.8 * mm});
            skCircle(sketch, "E37", {"center": v(35.44, -46.28) * mm, "radius": 0.8 * mm});
            skSolve(sketch);
        }
        {
            var Q0;
            {var subQ0=sQuery(id+"F12.wireOp",EDGE,"E24");Q0=makeQuery(id+"F12.imprint","IMPRINT",FACE,{"disambiguationData":[TD([[makeQuery(id+"F12.imprint","IMPRINT",EDGE,{"derivedFrom":subQ0}),-1.0]])]});}
            var Q1;
            {var subQ0=sQuery(id+"F12.wireOp",EDGE,"E27");var subQ5=sQuery(id+"F12.wireOp",EDGE,"E34");var subQ6=makeQuery(id+"F12.imprint","INTERSECT",VERTEX,{"disambiguationData":[OD(0.0)],"derivedFrom":[subQ0,subQ5]});Q1=makeQuery(id+"F12.imprint","IMPRINT",FACE,{"disambiguationData":[TD([[makeQuery(id+"F12.imprint","IMPRINT",EDGE,{"disambiguationData":[TD([[subQ6,-1.0]])],"derivedFrom":subQ5}),-1.0]])]});}
            var Q2;
            {var subQ0=sQuery(id+"F12.wireOp",EDGE,"E27");var subQ3=sQuery(id+"F12.wireOp",EDGE,"E30");var subQ5=makeQuery(id+"F12.imprint","INTERSECT",VERTEX,{"derivedFrom":[subQ0,subQ3]});Q2=makeQuery(id+"F12.imprint","IMPRINT",FACE,{"disambiguationData":[TD([[makeQuery(id+"F12.imprint","IMPRINT",EDGE,{"disambiguationData":[TD([[subQ5,-1.0]])],"derivedFrom":subQ3}),1.0]])]});}
            var Q3;
            {var subQ3=sQuery(id+"F12.wireOp",EDGE,"E34");var subQ5=sQuery(id+"F12.wireOp",EDGE,"E27");var subQ6=makeQuery(id+"F12.imprint","INTERSECT",VERTEX,{"disambiguationData":[OD(1.0)],"derivedFrom":[subQ5,subQ3]});Q3=makeQuery(id+"F12.imprint","IMPRINT",FACE,{"disambiguationData":[TD([[makeQuery(id+"F12.imprint","IMPRINT",EDGE,{"disambiguationData":[TD([[subQ6,-1.0]])],"derivedFrom":subQ5}),1.0]])]});}
            var Q4;
            {var subQ0=sQuery(id+"F12.wireOp",EDGE,"E34");var subQ1=sQuery(id+"F12.wireOp",EDGE,"E27");var subQ2=makeQuery(id+"F12.imprint","INTERSECT",VERTEX,{"disambiguationData":[OD(1.0)],"derivedFrom":[subQ1,subQ0]});Q4=makeQuery(id+"F12.imprint","IMPRINT",FACE,{"disambiguationData":[TD([[makeQuery(id+"F12.imprint","IMPRINT",EDGE,{"disambiguationData":[TD([[subQ2,-1.0]])],"derivedFrom":subQ1}),-1.0]])]});}
            var Q5;
            {var subQ1=sQuery(id+"F12.wireOp",EDGE,"E26");var subQ3=sQuery(id+"F12.wireOp",EDGE,"E30");var subQ4=makeQuery(id+"F12.imprint","INTERSECT",VERTEX,{"derivedFrom":[subQ1,subQ3]});Q5=makeQuery(id+"F12.imprint","IMPRINT",FACE,{"disambiguationData":[TD([[makeQuery(id+"F12.imprint","IMPRINT",EDGE,{"disambiguationData":[TD([[subQ4,-1.0]])],"derivedFrom":subQ3}),1.0]])]});}
            var Q6;
            {var subQ1=sQuery(id+"F12.wireOp",EDGE,"E26");var subQ3=sQuery(id+"F12.wireOp",EDGE,"E30");var subQ4=makeQuery(id+"F12.imprint","INTERSECT",VERTEX,{"derivedFrom":[subQ1,subQ3]});Q6=makeQuery(id+"F12.imprint","IMPRINT",FACE,{"disambiguationData":[TD([[makeQuery(id+"F12.imprint","IMPRINT",EDGE,{"disambiguationData":[TD([[subQ4,1.0]])],"derivedFrom":subQ3}),1.0]])]});}
            var Q7;
            {var subQ0=sQuery(id+"F12.wireOp",EDGE,"E30");var subQ1=sQuery(id+"F12.wireOp",EDGE,"E28");var subQ2=makeQuery(id+"F12.imprint","INTERSECT",VERTEX,{"derivedFrom":[subQ1,subQ0]});Q7=makeQuery(id+"F12.imprint","IMPRINT",FACE,{"disambiguationData":[TD([[makeQuery(id+"F12.imprint","IMPRINT",EDGE,{"disambiguationData":[TD([[subQ2,-1.0]])],"derivedFrom":subQ1}),-1.0]])]});}
            var Q8;
            {var subQ0=sQuery(id+"F12.wireOp",EDGE,"E30");var subQ3=sQuery(id+"F12.wireOp",EDGE,"E28");var subQ4=makeQuery(id+"F12.imprint","INTERSECT",VERTEX,{"derivedFrom":[subQ3,subQ0]});Q8=makeQuery(id+"F12.imprint","IMPRINT",FACE,{"disambiguationData":[TD([[makeQuery(id+"F12.imprint","IMPRINT",EDGE,{"disambiguationData":[TD([[subQ4,-1.0]])],"derivedFrom":subQ3}),1.0]])]});}
            var Q9;
            {var subQ0=sQuery(id+"F12.wireOp",EDGE,"E25");Q9=makeQuery(id+"F12.imprint","IMPRINT",FACE,{"disambiguationData":[TD([[makeQuery(id+"F12.imprint","IMPRINT",EDGE,{"derivedFrom":subQ0}),1.0]])]});}
            var Q10;
            {var subQ0=sQuery(id+"F12.wireOp",EDGE,"E28");var subQ5=sQuery(id+"F12.wireOp",EDGE,"E35");var subQ6=makeQuery(id+"F12.imprint","INTERSECT",VERTEX,{"disambiguationData":[OD(1.0)],"derivedFrom":[subQ0,subQ5]});Q10=makeQuery(id+"F12.imprint","IMPRINT",FACE,{"disambiguationData":[TD([[makeQuery(id+"F12.imprint","IMPRINT",EDGE,{"disambiguationData":[TD([[subQ6,1.0]])],"derivedFrom":subQ5}),-1.0]])]});}
            var Q11;
            {var subQ0=sQuery(id+"F12.wireOp",EDGE,"E29");var subQ1=sQuery(id+"F12.wireOp",EDGE,"E28");var subQ2=makeQuery(id+"F12.imprint","INTERSECT",VERTEX,{"derivedFrom":[subQ1,subQ0]});Q11=makeQuery(id+"F12.imprint","IMPRINT",FACE,{"disambiguationData":[TD([[makeQuery(id+"F12.imprint","IMPRINT",EDGE,{"disambiguationData":[TD([[subQ2,-1.0]])],"derivedFrom":subQ1}),-1.0]])]});}
            var Q12;
            {var subQ1=sQuery(id+"F12.wireOp",EDGE,"E28");var subQ3=sQuery(id+"F12.wireOp",EDGE,"E29");var subQ7=makeQuery(id+"F12.imprint","INTERSECT",VERTEX,{"derivedFrom":[subQ1,subQ3]});Q12=makeQuery(id+"F12.imprint","IMPRINT",FACE,{"disambiguationData":[TD([[makeQuery(id+"F12.imprint","IMPRINT",EDGE,{"disambiguationData":[TD([[subQ7,-1.0]])],"derivedFrom":subQ1}),1.0]])]});}
            var Q13;
            {var subQ0=sQuery(id+"F12.wireOp",EDGE,"E35");var subQ1=sQuery(id+"F12.wireOp",EDGE,"E28");var subQ2=makeQuery(id+"F12.imprint","INTERSECT",VERTEX,{"disambiguationData":[OD(0.0)],"derivedFrom":[subQ1,subQ0]});Q13=makeQuery(id+"F12.imprint","IMPRINT",FACE,{"disambiguationData":[TD([[makeQuery(id+"F12.imprint","IMPRINT",EDGE,{"disambiguationData":[TD([[subQ2,-1.0]])],"derivedFrom":subQ1}),1.0]])]});}
            var Q14;
            {var subQ0=sQuery(id+"F12.wireOp",EDGE,"E35");var subQ1=sQuery(id+"F12.wireOp",EDGE,"E28");var subQ2=makeQuery(id+"F12.imprint","INTERSECT",VERTEX,{"disambiguationData":[OD(0.0)],"derivedFrom":[subQ1,subQ0]});Q14=makeQuery(id+"F12.imprint","IMPRINT",FACE,{"disambiguationData":[TD([[makeQuery(id+"F12.imprint","IMPRINT",EDGE,{"disambiguationData":[TD([[subQ2,-1.0]])],"derivedFrom":subQ1}),-1.0]])]});}
            var Q15;
            {var subQ0=sQuery(id+"F12.wireOp",EDGE,"E28");var subQ3=sQuery(id+"F12.wireOp",EDGE,"E30");var subQ5=makeQuery(id+"F12.imprint","INTERSECT",VERTEX,{"derivedFrom":[subQ0,subQ3]});Q15=makeQuery(id+"F12.imprint","IMPRINT",FACE,{"disambiguationData":[TD([[makeQuery(id+"F12.imprint","IMPRINT",EDGE,{"disambiguationData":[TD([[subQ5,1.0]])],"derivedFrom":subQ3}),1.0]])]});}
            var Q16;
            {var subQ1=sQuery(id+"F12.wireOp",EDGE,"E31");var subQ5=sQuery(id+"F12.wireOp",EDGE,"E27");var subQ6=makeQuery(id+"F12.imprint","INTERSECT",VERTEX,{"derivedFrom":[subQ5,subQ1]});Q16=makeQuery(id+"F12.imprint","IMPRINT",FACE,{"disambiguationData":[TD([[makeQuery(id+"F12.imprint","IMPRINT",EDGE,{"disambiguationData":[TD([[subQ6,-1.0]])],"derivedFrom":subQ5}),1.0]])]});}
            var Q17;
            {var subQ0=sQuery(id+"F12.wireOp",EDGE,"E34");var subQ1=sQuery(id+"F12.wireOp",EDGE,"E27");var subQ2=makeQuery(id+"F12.imprint","INTERSECT",VERTEX,{"disambiguationData":[OD(0.0)],"derivedFrom":[subQ1,subQ0]});Q17=makeQuery(id+"F12.imprint","IMPRINT",FACE,{"disambiguationData":[TD([[makeQuery(id+"F12.imprint","IMPRINT",EDGE,{"disambiguationData":[TD([[subQ2,-1.0]])],"derivedFrom":subQ1}),1.0]])]});}
            var Q18;
            {var subQ0=sQuery(id+"F12.wireOp",EDGE,"E34");var subQ1=sQuery(id+"F12.wireOp",EDGE,"E27");var subQ2=makeQuery(id+"F12.imprint","INTERSECT",VERTEX,{"disambiguationData":[OD(0.0)],"derivedFrom":[subQ1,subQ0]});Q18=makeQuery(id+"F12.imprint","IMPRINT",FACE,{"disambiguationData":[TD([[makeQuery(id+"F12.imprint","IMPRINT",EDGE,{"disambiguationData":[TD([[subQ2,-1.0]])],"derivedFrom":subQ1}),-1.0]])]});}
            var Q19;
            {var subQ0=sQuery(id+"F12.wireOp",EDGE,"E31");var subQ1=sQuery(id+"F12.wireOp",EDGE,"E27");var subQ2=makeQuery(id+"F12.imprint","INTERSECT",VERTEX,{"derivedFrom":[subQ1,subQ0]});Q19=makeQuery(id+"F12.imprint","IMPRINT",FACE,{"disambiguationData":[TD([[makeQuery(id+"F12.imprint","IMPRINT",EDGE,{"disambiguationData":[TD([[subQ2,-1.0]])],"derivedFrom":subQ1}),-1.0]])]});}
            var Q20;
            {var subQ0=sQuery(id+"F12.wireOp",EDGE,"E24");Q20=makeQuery(id+"F12.imprint","IMPRINT",FACE,{"disambiguationData":[TD([[makeQuery(id+"F12.imprint","IMPRINT",EDGE,{"derivedFrom":subQ0}),1.0]])]});}
            var Q21;
            {var subQ0=sQuery(id+"F12.wireOp",EDGE,"E25");Q21=makeQuery(id+"F12.imprint","IMPRINT",FACE,{"disambiguationData":[TD([[makeQuery(id+"F12.imprint","IMPRINT",EDGE,{"derivedFrom":subQ0}),-1.0]])]});}
            var Q22;
            {var subQ0=sQuery(id+"F12.wireOp",EDGE,"E32");var subQ1=sQuery(id+"F12.wireOp",EDGE,"E23");var subQ2=makeQuery(id+"F12.imprint","INTERSECT",VERTEX,{"disambiguationData":[OD(0.0)],"derivedFrom":[subQ1,subQ0]});Q22=makeQuery(id+"F12.imprint","IMPRINT",FACE,{"disambiguationData":[TD([[makeQuery(id+"F12.imprint","IMPRINT",EDGE,{"disambiguationData":[TD([[subQ2,-1.0]])],"derivedFrom":subQ1}),1.0]])]});}
            var Q23;
            {var subQ0=sQuery(id+"F12.wireOp",EDGE,"E32");var subQ1=sQuery(id+"F12.wireOp",EDGE,"E23");var subQ2=makeQuery(id+"F12.imprint","INTERSECT",VERTEX,{"disambiguationData":[OD(0.0)],"derivedFrom":[subQ1,subQ0]});Q23=makeQuery(id+"F12.imprint","IMPRINT",FACE,{"disambiguationData":[TD([[makeQuery(id+"F12.imprint","IMPRINT",EDGE,{"disambiguationData":[TD([[subQ2,-1.0]])],"derivedFrom":subQ1}),-1.0]])]});}
            extrude(context, id + "F13", {"entities" : qUnion([Q0, Q1, Q2, Q3, Q4, Q5, Q6, Q7, Q8, Q9, Q10, Q11, Q12, Q13, Q14, Q15, Q16, Q17, Q18, Q19, Q20, Q21, Q22, Q23]), "flatOperationType" : FlatOperationType.REMOVE, "depth" : 6.35 * mm, "offsetDistance" : 25.4 * mm, "domain" : OperationDomain.MODEL});
        }
        {
            var Q0;
            {var subQ0=sQuery(id+"F12.wireOp",EDGE,"E32");var subQ1=sQuery(id+"F12.wireOp",EDGE,"E23");var subQ2=makeQuery(id+"F12.imprint","INTERSECT",VERTEX,{"disambiguationData":[OD(0.0)],"derivedFrom":[subQ1,subQ0]});Q0=makeQuery(id+"F12.imprint","IMPRINT",FACE,{"disambiguationData":[TD([[makeQuery(id+"F12.imprint","IMPRINT",EDGE,{"disambiguationData":[TD([[subQ2,-1.0]])],"derivedFrom":subQ1}),-1.0]])]});}
            var Q1;
            {var subQ0=sQuery(id+"F12.wireOp",EDGE,"E32");var subQ1=sQuery(id+"F12.wireOp",EDGE,"E23");var subQ2=makeQuery(id+"F12.imprint","INTERSECT",VERTEX,{"disambiguationData":[OD(0.0)],"derivedFrom":[subQ1,subQ0]});Q1=makeQuery(id+"F12.imprint","IMPRINT",FACE,{"disambiguationData":[TD([[makeQuery(id+"F12.imprint","IMPRINT",EDGE,{"disambiguationData":[TD([[subQ2,-1.0]])],"derivedFrom":subQ1}),1.0]])]});}
            var Q2;
            {var subQ0=sQuery(id+"F12.wireOp",EDGE,"E34");var subQ1=sQuery(id+"F12.wireOp",EDGE,"E27");var subQ2=makeQuery(id+"F12.imprint","INTERSECT",VERTEX,{"disambiguationData":[OD(0.0)],"derivedFrom":[subQ1,subQ0]});Q2=makeQuery(id+"F12.imprint","IMPRINT",FACE,{"disambiguationData":[TD([[makeQuery(id+"F12.imprint","IMPRINT",EDGE,{"disambiguationData":[TD([[subQ2,-1.0]])],"derivedFrom":subQ1}),-1.0]])]});}
            var Q3;
            {var subQ0=sQuery(id+"F12.wireOp",EDGE,"E34");var subQ1=sQuery(id+"F12.wireOp",EDGE,"E27");var subQ2=makeQuery(id+"F12.imprint","INTERSECT",VERTEX,{"disambiguationData":[OD(0.0)],"derivedFrom":[subQ1,subQ0]});Q3=makeQuery(id+"F12.imprint","IMPRINT",FACE,{"disambiguationData":[TD([[makeQuery(id+"F12.imprint","IMPRINT",EDGE,{"disambiguationData":[TD([[subQ2,-1.0]])],"derivedFrom":subQ1}),1.0]])]});}
            var Q4;
            {var subQ1=sQuery(id+"F12.wireOp",EDGE,"E31");var subQ5=sQuery(id+"F12.wireOp",EDGE,"E27");var subQ6=makeQuery(id+"F12.imprint","INTERSECT",VERTEX,{"derivedFrom":[subQ5,subQ1]});Q4=makeQuery(id+"F12.imprint","IMPRINT",FACE,{"disambiguationData":[TD([[makeQuery(id+"F12.imprint","IMPRINT",EDGE,{"disambiguationData":[TD([[subQ6,-1.0]])],"derivedFrom":subQ5}),1.0]])]});}
            var Q5;
            {var subQ0=sQuery(id+"F12.wireOp",EDGE,"E31");var subQ1=sQuery(id+"F12.wireOp",EDGE,"E27");var subQ2=makeQuery(id+"F12.imprint","INTERSECT",VERTEX,{"derivedFrom":[subQ1,subQ0]});Q5=makeQuery(id+"F12.imprint","IMPRINT",FACE,{"disambiguationData":[TD([[makeQuery(id+"F12.imprint","IMPRINT",EDGE,{"disambiguationData":[TD([[subQ2,-1.0]])],"derivedFrom":subQ1}),-1.0]])]});}
            var Q6;
            {var subQ0=sQuery(id+"F12.wireOp",EDGE,"E35");var subQ1=sQuery(id+"F12.wireOp",EDGE,"E28");var subQ2=makeQuery(id+"F12.imprint","INTERSECT",VERTEX,{"disambiguationData":[OD(0.0)],"derivedFrom":[subQ1,subQ0]});Q6=makeQuery(id+"F12.imprint","IMPRINT",FACE,{"disambiguationData":[TD([[makeQuery(id+"F12.imprint","IMPRINT",EDGE,{"disambiguationData":[TD([[subQ2,-1.0]])],"derivedFrom":subQ1}),1.0]])]});}
            var Q7;
            {var subQ1=sQuery(id+"F12.wireOp",EDGE,"E28");var subQ3=sQuery(id+"F12.wireOp",EDGE,"E29");var subQ7=makeQuery(id+"F12.imprint","INTERSECT",VERTEX,{"derivedFrom":[subQ1,subQ3]});Q7=makeQuery(id+"F12.imprint","IMPRINT",FACE,{"disambiguationData":[TD([[makeQuery(id+"F12.imprint","IMPRINT",EDGE,{"disambiguationData":[TD([[subQ7,-1.0]])],"derivedFrom":subQ1}),1.0]])]});}
            var Q8;
            {var subQ0=sQuery(id+"F12.wireOp",EDGE,"E29");var subQ1=sQuery(id+"F12.wireOp",EDGE,"E28");var subQ2=makeQuery(id+"F12.imprint","INTERSECT",VERTEX,{"derivedFrom":[subQ1,subQ0]});Q8=makeQuery(id+"F12.imprint","IMPRINT",FACE,{"disambiguationData":[TD([[makeQuery(id+"F12.imprint","IMPRINT",EDGE,{"disambiguationData":[TD([[subQ2,-1.0]])],"derivedFrom":subQ1}),-1.0]])]});}
            var Q9;
            {var subQ0=sQuery(id+"F12.wireOp",EDGE,"E35");var subQ1=sQuery(id+"F12.wireOp",EDGE,"E28");var subQ2=makeQuery(id+"F12.imprint","INTERSECT",VERTEX,{"disambiguationData":[OD(0.0)],"derivedFrom":[subQ1,subQ0]});Q9=makeQuery(id+"F12.imprint","IMPRINT",FACE,{"disambiguationData":[TD([[makeQuery(id+"F12.imprint","IMPRINT",EDGE,{"disambiguationData":[TD([[subQ2,-1.0]])],"derivedFrom":subQ1}),-1.0]])]});}
            extrude(context, id + "F14", {"entities" : qUnion([Q0, Q1, Q2, Q3, Q4, Q5, Q6, Q7, Q8, Q9]), "operationType" : NewBodyOperationType.REMOVE, "depth" : 1.59 * mm, "offsetDistance" : 25.4 * mm});
        }
        {
            var Q0;
            Q0=qCreatedBy(makeId("Front.planeOp"),FACE);
            var sketch = newSketch(context, id + "F15", { "sketchPlane" : qUnion([Q0])});
            skCircle(sketch, "E38", {"center": v(-43.8, -32.74) * mm, "radius": 12.7 * mm});
            skCircle(sketch, "E39", {"center": v(-43.8, -32.74) * mm, "radius": 15.88 * mm});
            skLineSegment(sketch, "E40", {"start": v(-43.8, -32.74) * mm, "end": v(-31.1, -32.74) * mm});
            skLineSegment(sketch, "E41", {"start": v(-31.1, -32.74) * mm, "end": v(-43.8, -32.74) * mm});
            skLineSegment(sketch, "E42", {"start": v(-43.8, -20.04) * mm, "end": v(-43.8, -32.74) * mm});
            skLineSegment(sketch, "E43", {"start": v(-43.8, -45.44) * mm, "end": v(-43.8, -32.74) * mm});
            skLineSegment(sketch, "E44", {"start": v(-56.5, -32.74) * mm, "end": v(-43.8, -32.74) * mm});
            skLineSegment(sketch, "E45", {"start": v(-43.8, -20.04) * mm, "end": v(-56.5, -32.74) * mm});
            skLineSegment(sketch, "E46", {"start": v(-56.5, -32.74) * mm, "end": v(-43.8, -45.44) * mm});
            skLineSegment(sketch, "E47", {"start": v(-43.8, -32.74) * mm, "end": v(-52.77, -41.72) * mm});
            skLineSegment(sketch, "E48", {"start": v(-52.77, -23.76) * mm, "end": v(-43.8, -32.74) * mm});
            skCircle(sketch, "E49", {"center": v(-37.44, -32.74) * mm, "radius": 1.59 * mm});
            skCircle(sketch, "E50", {"center": v(-49.27, -27.26) * mm, "radius": 1.59 * mm});
            skCircle(sketch, "E51", {"center": v(-49.27, -38.2) * mm, "radius": 1.59 * mm});
            skCircle(sketch, "E52", {"center": v(-43.8, -32.74) * mm, "radius": 4.45 * mm});
            skCircle(sketch, "E53", {"center": v(-43.8, -32.74) * mm, "radius": 3.18 * mm});
            skSolve(sketch);
        }
        {
            var Q0;
            {var subQ1=sQuery(id+"F15.wireOp",EDGE,"E38");var subQ3=sQuery(id+"F15.wireOp",EDGE,"E48");var subQ4=makeQuery(id+"F15.imprint","INTERSECT",VERTEX,{"derivedFrom":[subQ1,subQ3]});Q0=makeQuery(id+"F15.imprint","IMPRINT",FACE,{"disambiguationData":[TD([[makeQuery(id+"F15.imprint","IMPRINT",EDGE,{"disambiguationData":[TD([[subQ4,-1.0]])],"derivedFrom":subQ3}),1.0]])]});}
            var Q1;
            {var subQ1=sQuery(id+"F15.wireOp",EDGE,"E38");var subQ3=sQuery(id+"F15.wireOp",EDGE,"E48");var subQ4=makeQuery(id+"F15.imprint","INTERSECT",VERTEX,{"derivedFrom":[subQ1,subQ3]});Q1=makeQuery(id+"F15.imprint","IMPRINT",FACE,{"disambiguationData":[TD([[makeQuery(id+"F15.imprint","IMPRINT",EDGE,{"disambiguationData":[TD([[subQ4,-1.0]])],"derivedFrom":subQ3}),-1.0]])]});}
            var Q2;
            {var subQ0=sQuery(id+"F15.wireOp",EDGE,"E47");var subQ7=sQuery(id+"F15.wireOp",EDGE,"E52");var subQ9=makeQuery(id+"F15.imprint","INTERSECT",VERTEX,{"derivedFrom":[subQ0,subQ7]});Q2=makeQuery(id+"F15.imprint","IMPRINT",FACE,{"disambiguationData":[TD([[makeQuery(id+"F15.imprint","IMPRINT",EDGE,{"disambiguationData":[TD([[subQ9,-1.0]])],"derivedFrom":subQ0}),-1.0]])]});}
            var Q3;
            {var subQ1=sQuery(id+"F15.wireOp",EDGE,"E38");var subQ3=sQuery(id+"F15.wireOp",EDGE,"E47");var subQ4=makeQuery(id+"F15.imprint","INTERSECT",VERTEX,{"derivedFrom":[subQ1,subQ3]});Q3=makeQuery(id+"F15.imprint","IMPRINT",FACE,{"disambiguationData":[TD([[makeQuery(id+"F15.imprint","IMPRINT",EDGE,{"disambiguationData":[TD([[subQ4,1.0]])],"derivedFrom":subQ3}),-1.0]])]});}
            var Q4;
            {var subQ1=sQuery(id+"F15.wireOp",EDGE,"E38");var subQ3=sQuery(id+"F15.wireOp",EDGE,"E47");var subQ4=makeQuery(id+"F15.imprint","INTERSECT",VERTEX,{"derivedFrom":[subQ1,subQ3]});Q4=makeQuery(id+"F15.imprint","IMPRINT",FACE,{"disambiguationData":[TD([[makeQuery(id+"F15.imprint","IMPRINT",EDGE,{"disambiguationData":[TD([[subQ4,1.0]])],"derivedFrom":subQ3}),1.0]])]});}
            var Q5;
            {var subQ0=sQuery(id+"F15.wireOp",EDGE,"E52");var subQ1=sQuery(id+"F15.wireOp",EDGE,"E47");var subQ2=makeQuery(id+"F15.imprint","INTERSECT",VERTEX,{"derivedFrom":[subQ1,subQ0]});Q5=makeQuery(id+"F15.imprint","IMPRINT",FACE,{"disambiguationData":[TD([[makeQuery(id+"F15.imprint","IMPRINT",EDGE,{"disambiguationData":[TD([[subQ2,-1.0]])],"derivedFrom":subQ1}),1.0]])]});}
            var Q6;
            {var subQ1=sQuery(id+"F15.wireOp",EDGE,"E38");var subQ5=sQuery(id+"F15.wireOp",EDGE,"E41");var subQ9=makeQuery(id+"F15.imprint","INTERSECT",VERTEX,{"derivedFrom":[subQ1,subQ5]});Q6=makeQuery(id+"F15.imprint","IMPRINT",FACE,{"disambiguationData":[TD([[makeQuery(id+"F15.imprint","IMPRINT",EDGE,{"disambiguationData":[TD([[subQ9,-1.0]])],"derivedFrom":subQ5}),1.0]])]});}
            var Q7;
            {var subQ0=sQuery(id+"F15.wireOp",EDGE,"E52");var subQ1=sQuery(id+"F15.wireOp",EDGE,"E43");var subQ2=makeQuery(id+"F15.imprint","INTERSECT",VERTEX,{"derivedFrom":[subQ1,subQ0]});Q7=makeQuery(id+"F15.imprint","IMPRINT",FACE,{"disambiguationData":[TD([[makeQuery(id+"F15.imprint","IMPRINT",EDGE,{"disambiguationData":[TD([[subQ2,-1.0]])],"derivedFrom":subQ1}),1.0]])]});}
            var Q8;
            {var subQ0=sQuery(id+"F15.wireOp",EDGE,"E52");var subQ1=sQuery(id+"F15.wireOp",EDGE,"E41");var subQ2=makeQuery(id+"F15.imprint","INTERSECT",VERTEX,{"derivedFrom":[subQ1,subQ0]});Q8=makeQuery(id+"F15.imprint","IMPRINT",FACE,{"disambiguationData":[TD([[makeQuery(id+"F15.imprint","IMPRINT",EDGE,{"disambiguationData":[TD([[subQ2,-1.0]])],"derivedFrom":subQ1}),1.0]])]});}
            var Q9;
            {var subQ0=sQuery(id+"F15.wireOp",EDGE,"E52");var subQ1=sQuery(id+"F15.wireOp",EDGE,"E44");var subQ2=makeQuery(id+"F15.imprint","INTERSECT",VERTEX,{"derivedFrom":[subQ1,subQ0]});Q9=makeQuery(id+"F15.imprint","IMPRINT",FACE,{"disambiguationData":[TD([[makeQuery(id+"F15.imprint","IMPRINT",EDGE,{"disambiguationData":[TD([[subQ2,-1.0]])],"derivedFrom":subQ1}),-1.0]])]});}
            var Q10;
            {var subQ0=sQuery(id+"F15.wireOp",EDGE,"E52");var subQ1=sQuery(id+"F15.wireOp",EDGE,"E44");var subQ2=makeQuery(id+"F15.imprint","INTERSECT",VERTEX,{"derivedFrom":[subQ1,subQ0]});Q10=makeQuery(id+"F15.imprint","IMPRINT",FACE,{"disambiguationData":[TD([[makeQuery(id+"F15.imprint","IMPRINT",EDGE,{"disambiguationData":[TD([[subQ2,-1.0]])],"derivedFrom":subQ1}),1.0]])]});}
            var Q11;
            {var subQ0=sQuery(id+"F15.wireOp",EDGE,"E52");var subQ1=sQuery(id+"F15.wireOp",EDGE,"E42");var subQ2=makeQuery(id+"F15.imprint","INTERSECT",VERTEX,{"derivedFrom":[subQ1,subQ0]});Q11=makeQuery(id+"F15.imprint","IMPRINT",FACE,{"disambiguationData":[TD([[makeQuery(id+"F15.imprint","IMPRINT",EDGE,{"disambiguationData":[TD([[subQ2,-1.0]])],"derivedFrom":subQ1}),-1.0]])]});}
            var Q12;
            {var subQ0=sQuery(id+"F15.wireOp",EDGE,"E52");var subQ1=sQuery(id+"F15.wireOp",EDGE,"E41");var subQ2=makeQuery(id+"F15.imprint","INTERSECT",VERTEX,{"derivedFrom":[subQ1,subQ0]});Q12=makeQuery(id+"F15.imprint","IMPRINT",FACE,{"disambiguationData":[TD([[makeQuery(id+"F15.imprint","IMPRINT",EDGE,{"disambiguationData":[TD([[subQ2,-1.0]])],"derivedFrom":subQ1}),-1.0]])]});}
            var Q13;
            {var subQ1=sQuery(id+"F15.wireOp",EDGE,"E41");var subQ3=sQuery(id+"F15.wireOp",EDGE,"E53");var subQ4=makeQuery(id+"F15.imprint","INTERSECT",VERTEX,{"derivedFrom":[subQ1,subQ3]});Q13=makeQuery(id+"F15.imprint","IMPRINT",FACE,{"disambiguationData":[TD([[makeQuery(id+"F15.imprint","IMPRINT",EDGE,{"disambiguationData":[TD([[subQ4,-1.0]])],"derivedFrom":subQ3}),1.0]])]});}
            var Q14;
            {var subQ1=sQuery(id+"F15.wireOp",EDGE,"E42");var subQ3=sQuery(id+"F15.wireOp",EDGE,"E53");var subQ4=makeQuery(id+"F15.imprint","INTERSECT",VERTEX,{"derivedFrom":[subQ1,subQ3]});Q14=makeQuery(id+"F15.imprint","IMPRINT",FACE,{"disambiguationData":[TD([[makeQuery(id+"F15.imprint","IMPRINT",EDGE,{"disambiguationData":[TD([[subQ4,-1.0]])],"derivedFrom":subQ3}),1.0]])]});}
            var Q15;
            {var subQ1=sQuery(id+"F15.wireOp",EDGE,"E44");var subQ3=sQuery(id+"F15.wireOp",EDGE,"E53");var subQ4=makeQuery(id+"F15.imprint","INTERSECT",VERTEX,{"derivedFrom":[subQ1,subQ3]});Q15=makeQuery(id+"F15.imprint","IMPRINT",FACE,{"disambiguationData":[TD([[makeQuery(id+"F15.imprint","IMPRINT",EDGE,{"disambiguationData":[TD([[subQ4,1.0]])],"derivedFrom":subQ3}),1.0]])]});}
            var Q16;
            {var subQ1=sQuery(id+"F15.wireOp",EDGE,"E44");var subQ3=sQuery(id+"F15.wireOp",EDGE,"E53");var subQ4=makeQuery(id+"F15.imprint","INTERSECT",VERTEX,{"derivedFrom":[subQ1,subQ3]});Q16=makeQuery(id+"F15.imprint","IMPRINT",FACE,{"disambiguationData":[TD([[makeQuery(id+"F15.imprint","IMPRINT",EDGE,{"disambiguationData":[TD([[subQ4,-1.0]])],"derivedFrom":subQ3}),1.0]])]});}
            var Q17;
            {var subQ1=sQuery(id+"F15.wireOp",EDGE,"E43");var subQ3=sQuery(id+"F15.wireOp",EDGE,"E53");var subQ4=makeQuery(id+"F15.imprint","INTERSECT",VERTEX,{"derivedFrom":[subQ1,subQ3]});Q17=makeQuery(id+"F15.imprint","IMPRINT",FACE,{"disambiguationData":[TD([[makeQuery(id+"F15.imprint","IMPRINT",EDGE,{"disambiguationData":[TD([[subQ4,1.0]])],"derivedFrom":subQ3}),1.0]])]});}
            var Q18;
            {var subQ1=sQuery(id+"F15.wireOp",EDGE,"E41");var subQ3=sQuery(id+"F15.wireOp",EDGE,"E53");var subQ4=makeQuery(id+"F15.imprint","INTERSECT",VERTEX,{"derivedFrom":[subQ1,subQ3]});Q18=makeQuery(id+"F15.imprint","IMPRINT",FACE,{"disambiguationData":[TD([[makeQuery(id+"F15.imprint","IMPRINT",EDGE,{"disambiguationData":[TD([[subQ4,1.0]])],"derivedFrom":subQ3}),1.0]])]});}
            var Q19;
            {var subQ1=sQuery(id+"F15.wireOp",EDGE,"E41");var subQ6=sQuery(id+"F15.wireOp",EDGE,"E38");var subQ9=makeQuery(id+"F15.imprint","INTERSECT",VERTEX,{"derivedFrom":[subQ6,subQ1]});Q19=makeQuery(id+"F15.imprint","IMPRINT",FACE,{"disambiguationData":[TD([[makeQuery(id+"F15.imprint","IMPRINT",EDGE,{"disambiguationData":[TD([[subQ9,-1.0]])],"derivedFrom":subQ1}),-1.0]])]});}
            var Q20;
            {var subQ0=sQuery(id+"F15.wireOp",EDGE,"E50");var subQ3=sQuery(id+"F15.wireOp",EDGE,"E48");var subQ4=makeQuery(id+"F15.imprint","INTERSECT",VERTEX,{"disambiguationData":[OD(1.0)],"derivedFrom":[subQ3,subQ0]});Q20=makeQuery(id+"F15.imprint","IMPRINT",FACE,{"disambiguationData":[TD([[makeQuery(id+"F15.imprint","IMPRINT",EDGE,{"disambiguationData":[TD([[subQ4,-1.0]])],"derivedFrom":subQ3}),-1.0]])]});}
            var Q21;
            {var subQ0=sQuery(id+"F15.wireOp",EDGE,"E50");var subQ1=sQuery(id+"F15.wireOp",EDGE,"E48");var subQ2=makeQuery(id+"F15.imprint","INTERSECT",VERTEX,{"disambiguationData":[OD(1.0)],"derivedFrom":[subQ1,subQ0]});Q21=makeQuery(id+"F15.imprint","IMPRINT",FACE,{"disambiguationData":[TD([[makeQuery(id+"F15.imprint","IMPRINT",EDGE,{"disambiguationData":[TD([[subQ2,-1.0]])],"derivedFrom":subQ1}),1.0]])]});}
            extrude(context, id + "F16", {"entities" : qUnion([Q0, Q1, Q2, Q3, Q4, Q5, Q6, Q7, Q8, Q9, Q10, Q11, Q12, Q13, Q14, Q15, Q16, Q17, Q18, Q19, Q20, Q21]), "depth" : 1.59 * mm, "offsetDistance" : 25.4 * mm});
        }
        {
            var Q0;
            Q0=makeQuery(id+"F15.imprint","IMPRINT",FACE,{"disambiguationData":[TD([[makeQuery(id+"F15.imprint","IMPRINT",EDGE,{"derivedFrom":sQuery(id+"F15.wireOp",EDGE,"E39")}),1.0]])]});
            extrude(context, id + "F17", {"entities" : qUnion([Q0]), "operationType" : NewBodyOperationType.ADD, "depth" : 12.7 * mm, "offsetDistance" : 25.4 * mm});
        }
        {
            var Q0;
            {var subQ0=sQuery(id+"F15.wireOp",EDGE,"E52");var subQ1=sQuery(id+"F15.wireOp",EDGE,"E41");var subQ2=makeQuery(id+"F15.imprint","INTERSECT",VERTEX,{"derivedFrom":[subQ1,subQ0]});Q0=makeQuery(id+"F15.imprint","IMPRINT",FACE,{"disambiguationData":[TD([[makeQuery(id+"F15.imprint","IMPRINT",EDGE,{"disambiguationData":[TD([[subQ2,-1.0]])],"derivedFrom":subQ1}),1.0]])]});}
            var Q1;
            {var subQ0=sQuery(id+"F15.wireOp",EDGE,"E52");var subQ1=sQuery(id+"F15.wireOp",EDGE,"E41");var subQ2=makeQuery(id+"F15.imprint","INTERSECT",VERTEX,{"derivedFrom":[subQ1,subQ0]});Q1=makeQuery(id+"F15.imprint","IMPRINT",FACE,{"disambiguationData":[TD([[makeQuery(id+"F15.imprint","IMPRINT",EDGE,{"disambiguationData":[TD([[subQ2,-1.0]])],"derivedFrom":subQ1}),-1.0]])]});}
            var Q2;
            {var subQ0=sQuery(id+"F15.wireOp",EDGE,"E52");var subQ1=sQuery(id+"F15.wireOp",EDGE,"E42");var subQ2=makeQuery(id+"F15.imprint","INTERSECT",VERTEX,{"derivedFrom":[subQ1,subQ0]});Q2=makeQuery(id+"F15.imprint","IMPRINT",FACE,{"disambiguationData":[TD([[makeQuery(id+"F15.imprint","IMPRINT",EDGE,{"disambiguationData":[TD([[subQ2,-1.0]])],"derivedFrom":subQ1}),-1.0]])]});}
            var Q3;
            {var subQ0=sQuery(id+"F15.wireOp",EDGE,"E52");var subQ1=sQuery(id+"F15.wireOp",EDGE,"E44");var subQ2=makeQuery(id+"F15.imprint","INTERSECT",VERTEX,{"derivedFrom":[subQ1,subQ0]});Q3=makeQuery(id+"F15.imprint","IMPRINT",FACE,{"disambiguationData":[TD([[makeQuery(id+"F15.imprint","IMPRINT",EDGE,{"disambiguationData":[TD([[subQ2,-1.0]])],"derivedFrom":subQ1}),1.0]])]});}
            var Q4;
            {var subQ0=sQuery(id+"F15.wireOp",EDGE,"E52");var subQ1=sQuery(id+"F15.wireOp",EDGE,"E44");var subQ2=makeQuery(id+"F15.imprint","INTERSECT",VERTEX,{"derivedFrom":[subQ1,subQ0]});Q4=makeQuery(id+"F15.imprint","IMPRINT",FACE,{"disambiguationData":[TD([[makeQuery(id+"F15.imprint","IMPRINT",EDGE,{"disambiguationData":[TD([[subQ2,-1.0]])],"derivedFrom":subQ1}),-1.0]])]});}
            var Q5;
            {var subQ0=sQuery(id+"F15.wireOp",EDGE,"E52");var subQ1=sQuery(id+"F15.wireOp",EDGE,"E43");var subQ2=makeQuery(id+"F15.imprint","INTERSECT",VERTEX,{"derivedFrom":[subQ1,subQ0]});Q5=makeQuery(id+"F15.imprint","IMPRINT",FACE,{"disambiguationData":[TD([[makeQuery(id+"F15.imprint","IMPRINT",EDGE,{"disambiguationData":[TD([[subQ2,-1.0]])],"derivedFrom":subQ1}),1.0]])]});}
            var Q6;
            Q6=sQuery(id+"F15.wireOp",EDGE,"E52");
            var Q7;
            Q7=sQuery(id+"F15.wireOp",EDGE,"E53");
            extrude(context, id + "F18", {"entities" : qUnion([Q0, Q1, Q2, Q3, Q4, Q5]), "operationType" : NewBodyOperationType.ADD, "surfaceEntities" : qUnion([Q6, Q7]), "oppositeDirection" : true, "depth" : 6.35 * mm, "offsetDistance" : 25.4 * mm});
        }
        {
            var Q0;
            Q0=qCreatedBy(makeId("Top.planeOp"),FACE);
            var sketch = newSketch(context, id + "F19", { "sketchPlane" : qUnion([Q0])});
            skLineSegment(sketch, "E54", {"start": v(-43.8, 0) * mm, "end": v(-43.8, -10.16) * mm});
            skLineSegment(sketch, "E55", {"start": v(-43.8, -10.16) * mm, "end": v(-43.8, 0) * mm});
            skLineSegment(sketch, "E56", {"start": v(-43.8, 0) * mm, "end": v(-43.8, 3.17) * mm});
            skSolve(sketch);
        }
        {
            var Q0;
            Q0=sQuery(id+"F19.wireOp",VERTEX,"E54.end");
            var Q1;
            Q1=makeQuery(id+"F16.opExtrude","SWEPT_BODY",BODY,{"disambiguationData":[OSD([sQuery(id+"F15.wireOp",EDGE,"E38"),sQuery(id+"F15.wireOp",EDGE,"E49"),sQuery(id+"F15.wireOp",EDGE,"E50"),sQuery(id+"F15.wireOp",EDGE,"E51")])]});
            hole(context, id + "F20", {"style" : HoleStyle.SIMPLE, "endStyle" : HoleEndStyle.BLIND, "standardTappedOrClearance" : lookupTablePath({ "standard" : "ANSI", "engagement" : "75%", "pitch" : "40 tpi", "size" : "#4", "type" : "Tapped" }), "standardBlindInLast" : lookupTablePath({ "standard" : "ANSI", "engagement" : "75%", "pitch" : "40 tpi", "size" : "#4", "type" : "Tapped" }), "holeDiameter" : 2.26 * mm, "majorDiameter" : 2.84 * mm, "showTappedDepth" : true, "holeDepth" : 8.76 * mm, "tappedDepth" : 6.86 * mm, "tapClearance" : 3, "locations" : qUnion([Q0]), "scope" : qUnion([Q1])});
        }
        {
            var Q0;
            Q0=sQuery(id+"F19.wireOp",VERTEX,"E56.end");
            var Q1;
            Q1=makeQuery(id+"F18.opExtrude","SWEPT_BODY",BODY,{"disambiguationData":[OSD([sQuery(id+"F15.wireOp",EDGE,"E52"),sQuery(id+"F15.wireOp",EDGE,"E53")])]});
            var Q2;
            Q2=makeQuery(id+"F16.opExtrude","SWEPT_BODY",BODY,{"disambiguationData":[OSD([sQuery(id+"F15.wireOp",EDGE,"E38"),sQuery(id+"F15.wireOp",EDGE,"E49"),sQuery(id+"F15.wireOp",EDGE,"E50"),sQuery(id+"F15.wireOp",EDGE,"E51")])]});
            hole(context, id + "F21", {"style" : HoleStyle.SIMPLE, "endStyle" : HoleEndStyle.THROUGH, "standardTappedOrClearance" : lookupTablePath({ "standard" : "ANSI", "engagement" : "75%", "pitch" : "40 tpi", "size" : "#4", "type" : "Tapped" }), "standardBlindInLast" : lookupTablePath({ "standard" : "ANSI", "engagement" : "75%", "pitch" : "40 tpi", "size" : "#4", "type" : "Tapped" }), "holeDiameter" : 2.26 * mm, "majorDiameter" : 2.84 * mm, "showTappedDepth" : true, "isTappedThrough" : true, "tappedDepth" : 6.86 * mm, "tapClearance" : 3, "locations" : qUnion([Q0]), "scope" : qUnion([Q1, Q2])});
        }
        {
            var Q0;
            Q0=qCreatedBy(makeId("Top.planeOp"),FACE);
            cPlane(context, id + "F22", {"entities" : qUnion([Q0]), "cplaneType" : CPlaneType.OFFSET, "offset" : 12.7 * mm, "width" : 152.4 * mm, "height" : 152.4 * mm});
        }
        {
            var Q0;
            Q0=qCreatedBy(id+"F22.planeOp",FACE);
            var sketch = newSketch(context, id + "F23", { "sketchPlane" : qUnion([Q0])});
            skLineSegment(sketch, "E57", {"start": v(0, 0) * mm, "end": v(0, -2.24) * mm});
            skSolve(sketch);
        }
        {
            var Q0;
            Q0=sQuery(id+"F23.wireOp",VERTEX,"E57.end");
            var Q1;
            Q1=makeQuery(id+"F1.opExtrude","SWEPT_BODY",BODY,{"disambiguationData":[OSD([sQuery(id+"F0.wireOp",EDGE,"E0")])]});
            hole(context, id + "F24", {"style" : HoleStyle.SIMPLE, "endStyle" : HoleEndStyle.BLIND, "standardTappedOrClearance" : lookupTablePath({ "standard" : "ANSI", "fit" : "Normal (ASME)", "size" : "#4", "type" : "Clearance" }), "standardBlindInLast" : lookupTablePath({ "fit" : "Free", "standard" : "ANSI", "size" : "#4", "type" : "Clearance" }), "holeDiameter" : 3.26 * mm, "majorDiameter" : 2.84 * mm, "holeDepth" : 2.7 * mm, "tappedDepth" : 0.8 * mm, "tapClearance" : 3, "locations" : qUnion([Q0]), "scope" : qUnion([Q1])});
        }
        {
            var Q0;
            Q0=makeQuery(id+"F1.opExtrude","CAP_EDGE",EDGE,{"disambiguationData":[OSD([sQuery(id+"F0.wireOp",EDGE,"E0")])],"isStart":false});
            fillet(context, id + "F25", {"entities" : qUnion([Q0]), "radius" : 1.27 * mm, "tangentPropagation" : true, "allowEdgeOverflow" : false});
        }
    });
